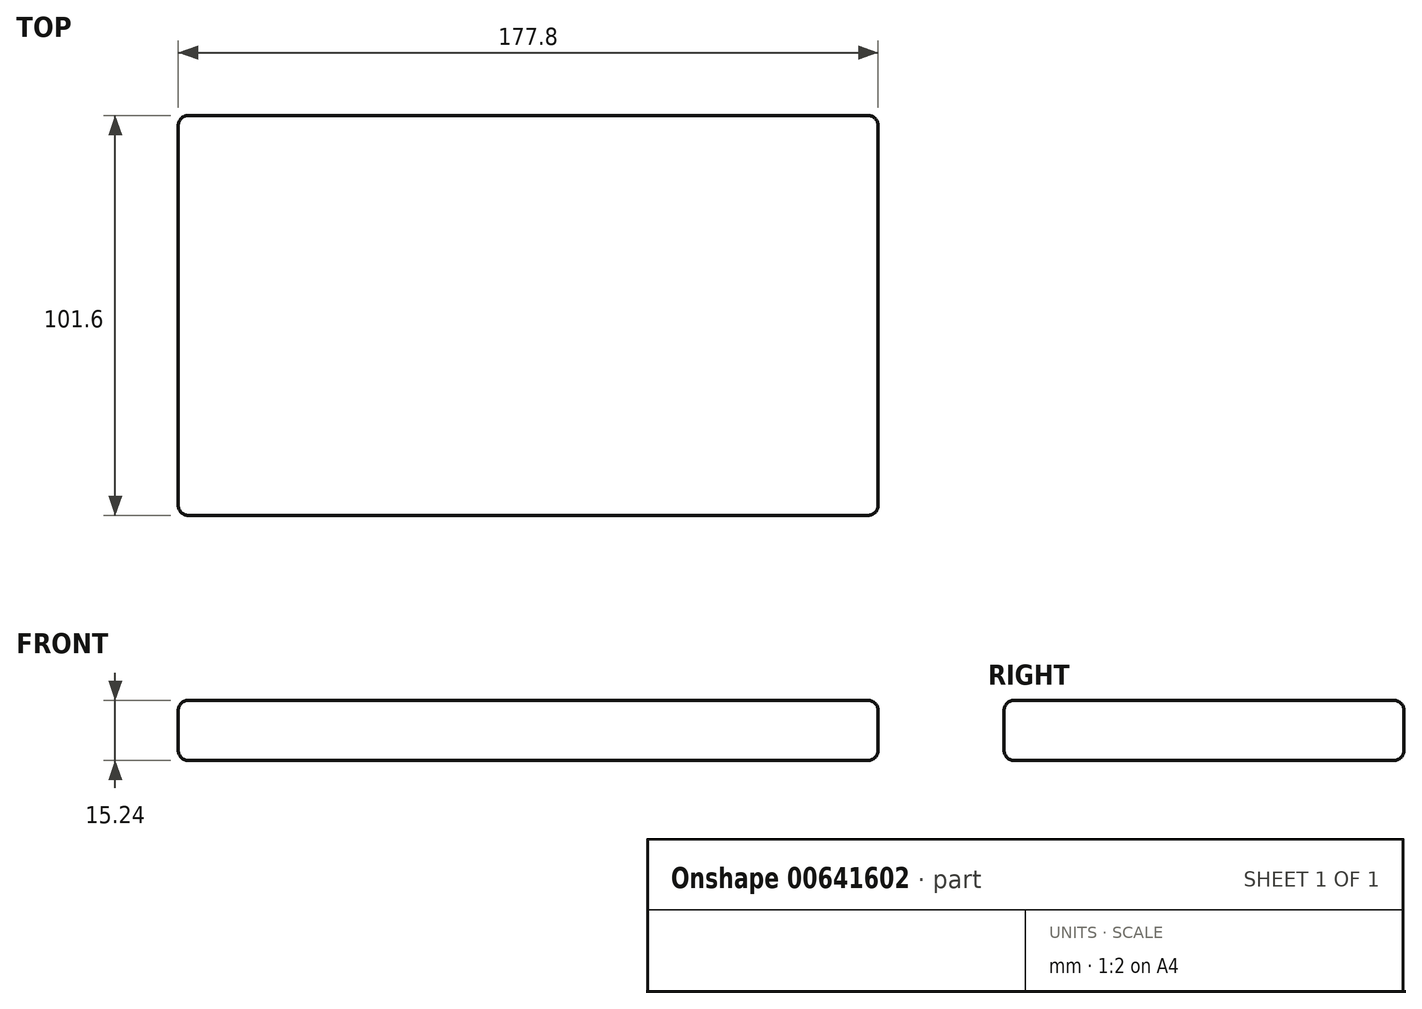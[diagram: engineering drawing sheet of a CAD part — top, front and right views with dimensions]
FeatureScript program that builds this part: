
annotation { "Feature Type Name" : "Feature", "Feature Type Description" : "" }
export const myFeature = defineFeature(function(context is Context, id is Id, definition is map)
    precondition{}
    {
        {
            var Q0;
            Q0=qCreatedBy(makeId("Top.planeOp"),FACE);
            var sketch = newSketch(context, id + "F0", { "sketchPlane" : qUnion([Q0])});
            skLineSegment(sketch, "E0", {"start": v(-105.92, 59.38) * mm, "end": v(-105.92, -42.22) * mm});
            skLineSegment(sketch, "E1", {"start": v(-105.92, -42.22) * mm, "end": v(71.88, -42.22) * mm});
            skLineSegment(sketch, "E2", {"start": v(71.88, -42.22) * mm, "end": v(71.88, 59.38) * mm});
            skLineSegment(sketch, "E3", {"start": v(71.88, 59.38) * mm, "end": v(-105.92, 59.38) * mm});
            skSolve(sketch);
        }
        {
            var Q0;
            Q0=makeQuery(id+"F0.imprint","IMPRINT",FACE,{"disambiguationData":[TD([[makeQuery(id+"F0.imprint","IMPRINT",EDGE,{"derivedFrom":sQuery(id+"F0.wireOp",EDGE,"E0")}),1.0]])]});
            extrude(context, id + "F1", {"entities" : qUnion([Q0]), "depth" : 15.24 * mm, "offsetDistance" : 25.4 * mm});
        }
        {
            var Q0;
            Q0=makeQuery(id+"F1.opExtrude","SWEPT_EDGE",EDGE,{"disambiguationData":[OSD([sQuery(id+"F0.wireOp",EDGE,"E2"),sQuery(id+"F0.wireOp",EDGE,"E3")])]});
            var Q1;
            Q1=makeQuery(id+"F1.opExtrude","SWEPT_EDGE",EDGE,{"disambiguationData":[OSD([sQuery(id+"F0.wireOp",EDGE,"E0"),sQuery(id+"F0.wireOp",EDGE,"E3")])]});
            var Q2;
            Q2=makeQuery(id+"F1.opExtrude","SWEPT_EDGE",EDGE,{"disambiguationData":[OSD([sQuery(id+"F0.wireOp",EDGE,"E1"),sQuery(id+"F0.wireOp",EDGE,"E2")])]});
            var Q3;
            Q3=makeQuery(id+"F1.opExtrude","SWEPT_EDGE",EDGE,{"disambiguationData":[OSD([sQuery(id+"F0.wireOp",EDGE,"E0"),sQuery(id+"F0.wireOp",EDGE,"E1")])]});
            var Q4;
            Q4=makeQuery(id+"F1.opExtrude","CAP_EDGE",EDGE,{"disambiguationData":[OSD([sQuery(id+"F0.wireOp",EDGE,"E0")])],"isStart":true});
            var Q5;
            Q5=makeQuery(id+"F1.opExtrude","CAP_EDGE",EDGE,{"disambiguationData":[OSD([sQuery(id+"F0.wireOp",EDGE,"E0")])],"isStart":false});
            var Q6;
            Q6=makeQuery(id+"F1.opExtrude","CAP_EDGE",EDGE,{"disambiguationData":[OSD([sQuery(id+"F0.wireOp",EDGE,"E3")])],"isStart":false});
            var Q7;
            Q7=makeQuery(id+"F1.opExtrude","CAP_EDGE",EDGE,{"disambiguationData":[OSD([sQuery(id+"F0.wireOp",EDGE,"E2")])],"isStart":false});
            var Q8;
            Q8=makeQuery(id+"F1.opExtrude","CAP_EDGE",EDGE,{"disambiguationData":[OSD([sQuery(id+"F0.wireOp",EDGE,"E1")])],"isStart":false});
            var Q9;
            Q9=makeQuery(id+"F1.opExtrude","CAP_EDGE",EDGE,{"disambiguationData":[OSD([sQuery(id+"F0.wireOp",EDGE,"E3")])],"isStart":true});
            var Q10;
            Q10=makeQuery(id+"F1.opExtrude","CAP_EDGE",EDGE,{"disambiguationData":[OSD([sQuery(id+"F0.wireOp",EDGE,"E1")])],"isStart":true});
            var Q11;
            Q11=makeQuery(id+"F1.opExtrude","CAP_EDGE",EDGE,{"disambiguationData":[OSD([sQuery(id+"F0.wireOp",EDGE,"E2")])],"isStart":true});
            fillet(context, id + "F2", {"entities" : qUnion([Q0, Q1, Q2, Q3, Q4, Q5, Q6, Q7, Q8, Q9, Q10, Q11]), "radius" : 2.54 * mm, "tangentPropagation" : true, "allowEdgeOverflow" : false});
        }
    });
